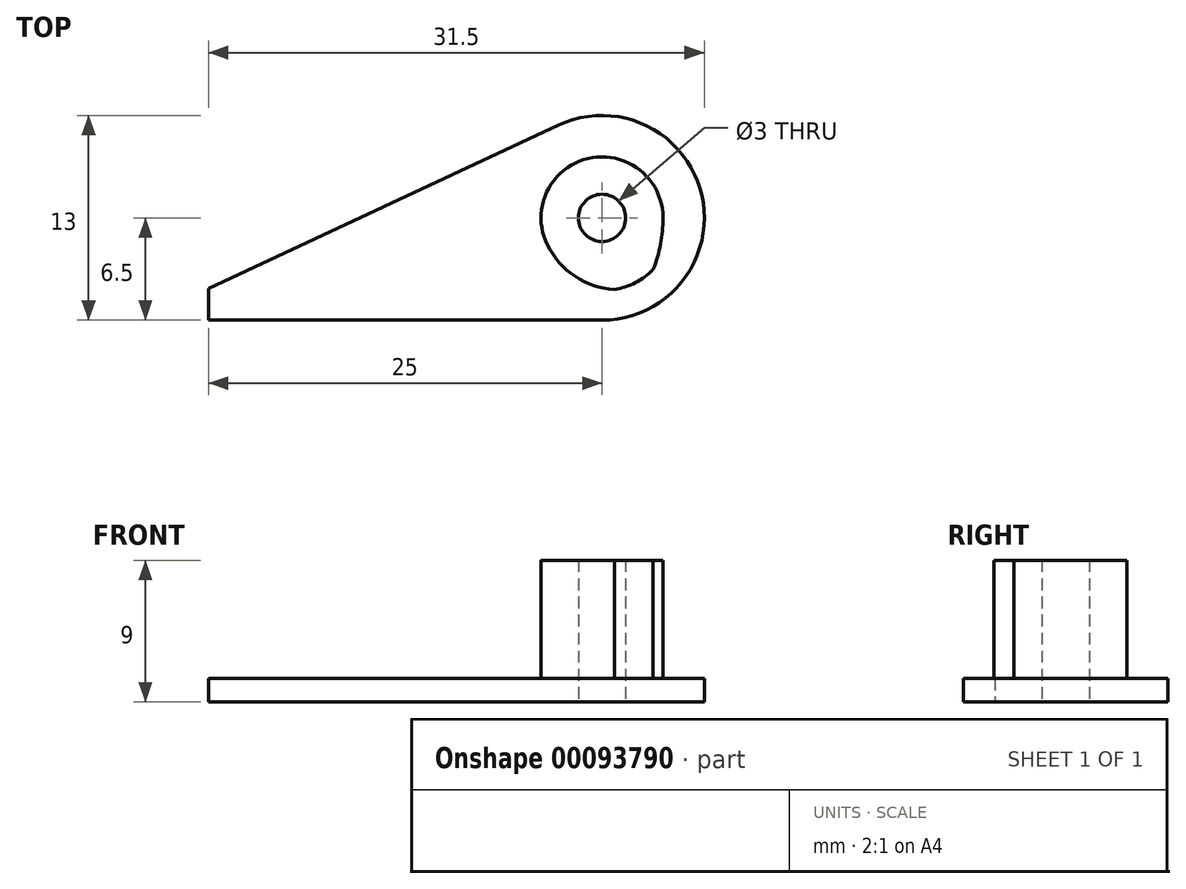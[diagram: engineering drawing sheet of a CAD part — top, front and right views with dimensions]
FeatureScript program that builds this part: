
annotation { "Feature Type Name" : "Feature", "Feature Type Description" : "" }
export const myFeature = defineFeature(function(context is Context, id is Id, definition is map)
    precondition{}
    {
        {
            var Q0;
            Q0=qCreatedBy(makeId("Top.planeOp"),FACE);
            var sketch = newSketch(context, id + "F0", { "sketchPlane" : qUnion([Q0])});
            skCircle(sketch, "E0", {"center": v(0, 0) * mm, "radius": 6.5 * mm});
            skCircle(sketch, "E1", {"center": v(0, 0) * mm, "radius": 1.5 * mm});
            skLineSegment(sketch, "E2", {"start": v(0, -6.5) * mm, "end": v(-25, -6.5) * mm});
            skLineSegment(sketch, "E3", {"start": v(-25, -6.5) * mm, "end": v(-25, -4.5) * mm});
            skLineSegment(sketch, "E4", {"start": v(-25, -4.5) * mm, "end": v(-2.75, 5.89) * mm});
            skCircle(sketch, "E5", {"center": v(0, 0) * mm, "radius": 4.62 * mm});
            skLineSegment(sketch, "E6", {"start": v(0, 0) * mm, "end": v(0, -4.62) * mm, "construction": true});
            skLineSegment(sketch, "E7", {"start": v(0, 0) * mm, "end": v(6.5, 0) * mm, "construction": true});
            skPoint(sketch, "E8", {"position": v(6.5, -6.5) * mm});
            skLineSegment(sketch, "E9", {"start": v(0, 0) * mm, "end": v(6.5, -6.5) * mm, "construction": true});
            skPoint(sketch, "E10", {"position": v(4.6, -4.6) * mm});
            skLineSegment(sketch, "E11", {"start": v(0, 0) * mm, "end": v(0, 6.5) * mm, "construction": true});
            skPoint(sketch, "E12", {"position": v(6.5, 6.5) * mm});
            skLineSegment(sketch, "E13", {"start": v(0, 0) * mm, "end": v(6.5, 6.5) * mm, "construction": true});
            skPoint(sketch, "E14", {"position": v(3.27, 3.27) * mm});
            skPoint(sketch, "E15", {"position": v(3.25, -3.3) * mm});
            skPoint(sketch, "E15.positionSnap0", {"position": v(3.25, -3.25) * mm});
            skPoint(sketch, "E16", {"position": v(4.62, 0) * mm});
            skPoint(sketch, "E17", {"position": v(3.88, 0) * mm});
            skArc(sketch, "E18", {"start": v(3.25, -3.3) * mm, "mid": v(3.87, -0.01) * mm, "end": v(3.27, 3.27) * mm});
            skArc(sketch, "E19", {"start": v(3.88, 0) * mm, "mid": v(-0.89, 3.77) * mm, "end": v(-3.47, -1.73) * mm});
            skArc(sketch, "E20", {"start": v(-3.47, -1.73) * mm, "mid": v(-1.72, -3.71) * mm, "end": v(0.78, -4.56) * mm});
            skSolve(sketch);
        }
        {
            var Q0;
            {var subQ0=sQuery(id+"F0.wireOp",EDGE,"E2");Q0=makeQuery(id+"F0.imprint","IMPRINT",FACE,{"disambiguationData":[TD([[makeQuery(id+"F0.imprint","IMPRINT",EDGE,{"derivedFrom":subQ0}),-1.0]])]});}
            var Q1;
            {var subQ0=sQuery(id+"F0.wireOp",EDGE,"E0");var subQ1=makeQuery(id+"F0.imprint","INTERSECT",VERTEX,{"derivedFrom":[subQ0,sQuery(id+"F0.wireOp",EDGE,"E2")]});Q1=makeQuery(id+"F0.imprint","IMPRINT",FACE,{"disambiguationData":[TD([[makeQuery(id+"F0.imprint","IMPRINT",EDGE,{"disambiguationData":[TD([[subQ1,1.0]])],"derivedFrom":subQ0}),1.0]])]});}
            var Q2;
            Q2=makeQuery(id+"F0.imprint","IMPRINT",FACE,{"disambiguationData":[TD([[makeQuery(id+"F0.imprint","IMPRINT",EDGE,{"derivedFrom":sQuery(id+"F0.wireOp",EDGE,"E1")}),-1.0]])]});
            var Q3;
            {var subQ0=sQuery(id+"F0.wireOp",EDGE,"E18");Q3=makeQuery(id+"F0.imprint","IMPRINT",FACE,{"disambiguationData":[TD([[makeQuery(id+"F0.imprint","IMPRINT",EDGE,{"derivedFrom":subQ0}),-1.0]])]});}
            var Q4;
            {var subQ4=sQuery(id+"F0.wireOp",EDGE,"E19");Q4=makeQuery(id+"F0.imprint","IMPRINT",FACE,{"disambiguationData":[TD([[makeQuery(id+"F0.imprint","IMPRINT",EDGE,{"derivedFrom":subQ4}),-1.0]])]});}
            extrude(context, id + "F1", {"entities" : qUnion([Q0, Q1, Q2, Q3, Q4]), "depth" : 1.5 * mm});
        }
        {
            var Q0;
            Q0=makeQuery(id+"F0.imprint","IMPRINT",FACE,{"disambiguationData":[TD([[makeQuery(id+"F0.imprint","IMPRINT",EDGE,{"derivedFrom":sQuery(id+"F0.wireOp",EDGE,"E1")}),-1.0]])]});
            extrude(context, id + "F2", {"entities" : qUnion([Q0]), "operationType" : NewBodyOperationType.ADD, "depth" : 9 * mm});
        }
    });
